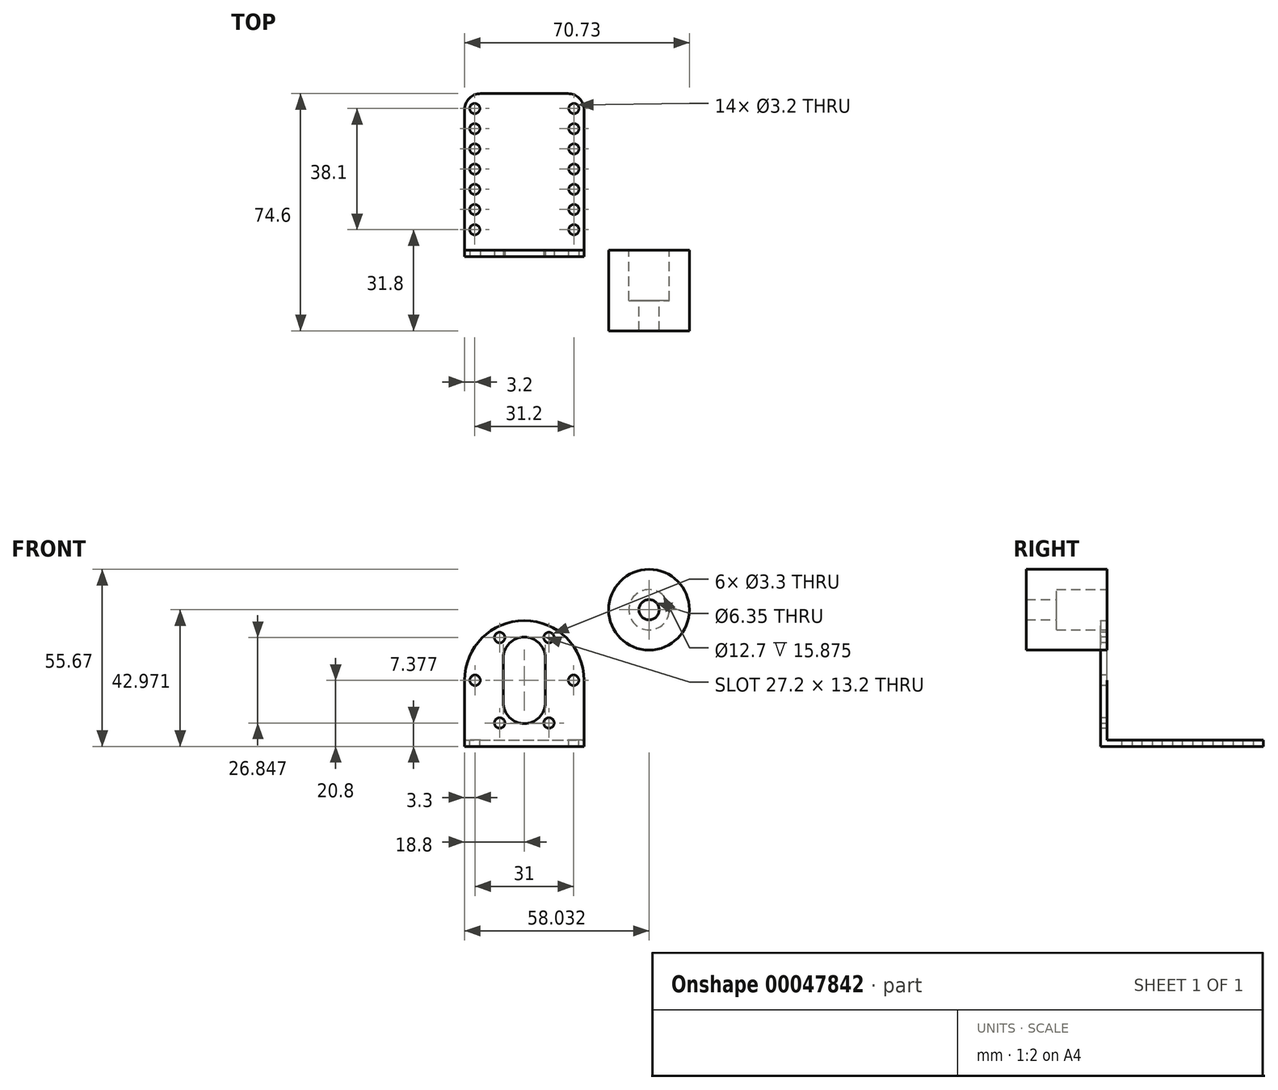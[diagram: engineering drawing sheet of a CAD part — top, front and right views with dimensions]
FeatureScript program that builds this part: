
annotation { "Feature Type Name" : "Feature", "Feature Type Description" : "" }
export const myFeature = defineFeature(function(context is Context, id is Id, definition is map)
    precondition{}
    {
        {
            var Q0;
            Q0=qCreatedBy(makeId("Front.planeOp"),FACE);
            var sketch = newSketch(context, id + "F0", { "sketchPlane" : qUnion([Q0])});
            skLineSegment(sketch, "E0.bottom", {"start": v(-18.8, 0) * mm, "end": v(18.8, 0) * mm});
            skLineSegment(sketch, "E0.top", {"start": v(-18.8, 18.8) * mm, "end": v(18.8, 18.8) * mm, "construction": true});
            skLineSegment(sketch, "E0.left", {"start": v(-18.8, 0) * mm, "end": v(-18.8, 18.8) * mm});
            skLineSegment(sketch, "E0.right", {"start": v(18.8, 0) * mm, "end": v(18.8, 18.8) * mm});
            skArc(sketch, "E1", {"start": v(18.8, 18.8) * mm, "mid": v(0, 37.6) * mm, "end": v(-18.8, 18.8) * mm});
            skSolve(sketch);
        }
        {
            var Q0;
            Q0=makeQuery(id+"F0.imprint","IMPRINT",FACE,{"disambiguationData":[TD([[makeQuery(id+"F0.imprint","IMPRINT",EDGE,{"derivedFrom":sQuery(id+"F0.wireOp",EDGE,"E0.bottom")}),1.0]])]});
            extrude(context, id + "F1", {"entities" : qUnion([Q0]), "depth" : 2 * mm});
        }
        {
            var Q0;
            Q0=makeQuery(id+"F1.opExtrude","CAP_FACE",FACE,{"disambiguationData":[OSD([sQuery(id+"F0.wireOp",EDGE,"E0.bottom"),sQuery(id+"F0.wireOp",EDGE,"E0.left"),sQuery(id+"F0.wireOp",EDGE,"E0.right"),sQuery(id+"F0.wireOp",EDGE,"E1")])],"isStart":false});
            var sketch = newSketch(context, id + "F2", { "sketchPlane" : qUnion([Q0])});
            skCircle(sketch, "E2", {"center": v(0, 18.8) * mm, "radius": 15.5 * mm, "construction": true});
            skLineSegment(sketch, "E3", {"start": v(-18.8, 18.8) * mm, "end": v(18.8, 18.8) * mm, "construction": true});
            skCircle(sketch, "E4", {"center": v(-15.5, 18.8) * mm, "radius": 1.65 * mm});
            skCircle(sketch, "E5.1.0", {"center": v(-7.75, 5.38) * mm, "radius": 1.65 * mm});
            skCircle(sketch, "E5.2.0", {"center": v(7.75, 5.38) * mm, "radius": 1.65 * mm});
            skCircle(sketch, "E5.3.0", {"center": v(15.5, 18.8) * mm, "radius": 1.65 * mm});
            skCircle(sketch, "E5.4.0", {"center": v(7.75, 32.22) * mm, "radius": 1.65 * mm});
            skCircle(sketch, "E5.5.0", {"center": v(-7.75, 32.22) * mm, "radius": 1.65 * mm});
            skSolve(sketch);
        }
        {
            var Q0;
            Q0=makeQuery(id+"F2.imprint","IMPRINT",FACE,{"disambiguationData":[TD([[makeQuery(id+"F2.imprint","IMPRINT",EDGE,{"derivedFrom":sQuery(id+"F2.wireOp",EDGE,"E4")}),1.0]])]});
            var Q1;
            Q1=makeQuery(id+"F2.imprint","IMPRINT",FACE,{"disambiguationData":[TD([[makeQuery(id+"F2.imprint","IMPRINT",EDGE,{"derivedFrom":sQuery(id+"F2.wireOp",EDGE,"E5.5.0")}),1.0]])]});
            var Q2;
            Q2=makeQuery(id+"F2.imprint","IMPRINT",FACE,{"disambiguationData":[TD([[makeQuery(id+"F2.imprint","IMPRINT",EDGE,{"derivedFrom":sQuery(id+"F2.wireOp",EDGE,"E5.4.0")}),1.0]])]});
            var Q3;
            Q3=makeQuery(id+"F2.imprint","IMPRINT",FACE,{"disambiguationData":[TD([[makeQuery(id+"F2.imprint","IMPRINT",EDGE,{"derivedFrom":sQuery(id+"F2.wireOp",EDGE,"E5.2.0")}),1.0]])]});
            var Q4;
            Q4=makeQuery(id+"F2.imprint","IMPRINT",FACE,{"disambiguationData":[TD([[makeQuery(id+"F2.imprint","IMPRINT",EDGE,{"derivedFrom":sQuery(id+"F2.wireOp",EDGE,"E5.1.0")}),1.0]])]});
            var Q5;
            Q5=makeQuery(id+"F2.imprint","IMPRINT",FACE,{"disambiguationData":[TD([[makeQuery(id+"F2.imprint","IMPRINT",EDGE,{"derivedFrom":sQuery(id+"F2.wireOp",EDGE,"E5.3.0")}),1.0]])]});
            extrude(context, id + "F3", {"entities" : qUnion([Q0, Q1, Q2, Q3, Q4, Q5]), "operationType" : NewBodyOperationType.REMOVE, "endBound" : BoundingType.UP_TO_NEXT, "oppositeDirection" : true, "depth" : 25.4 * mm});
        }
        {
            var Q0;
            Q0=makeQuery(id+"F1.opExtrude","CAP_FACE",FACE,{"disambiguationData":[OSD([sQuery(id+"F0.wireOp",EDGE,"E0.bottom"),sQuery(id+"F0.wireOp",EDGE,"E0.left"),sQuery(id+"F0.wireOp",EDGE,"E0.right"),sQuery(id+"F0.wireOp",EDGE,"E1")])],"isStart":false});
            var sketch = newSketch(context, id + "F4", { "sketchPlane" : qUnion([Q0])});
            skLineSegment(sketch, "E6.bottom", {"start": v(-6.6, 25.8) * mm, "end": v(6.6, 25.8) * mm, "construction": true});
            skLineSegment(sketch, "E6.top", {"start": v(-6.6, 11.8) * mm, "end": v(6.6, 11.8) * mm, "construction": true});
            skLineSegment(sketch, "E6.left", {"start": v(-6.6, 25.8) * mm, "end": v(-6.6, 11.8) * mm});
            skLineSegment(sketch, "E6.right", {"start": v(6.6, 25.8) * mm, "end": v(6.6, 11.8) * mm});
            skLineSegment(sketch, "E7", {"start": v(0, 25.8) * mm, "end": v(0, 11.8) * mm, "construction": true});
            skArc(sketch, "E8", {"start": v(6.6, 25.8) * mm, "mid": v(0, 32.4) * mm, "end": v(-6.6, 25.8) * mm});
            skArc(sketch, "E9", {"start": v(-6.6, 11.8) * mm, "mid": v(0, 5.2) * mm, "end": v(6.6, 11.8) * mm});
            skLineSegment(sketch, "E10", {"start": v(-6.6, 18.8) * mm, "end": v(6.6, 18.8) * mm, "construction": true});
            skLineSegment(sketch, "E11", {"start": v(-15.5, 18.8) * mm, "end": v(15.5, 18.8) * mm, "construction": true});
            skSolve(sketch);
        }
        {
            var Q0;
            Q0=makeQuery(id+"F4.imprint","IMPRINT",FACE,{"disambiguationData":[TD([[makeQuery(id+"F4.imprint","IMPRINT",EDGE,{"derivedFrom":sQuery(id+"F4.wireOp",EDGE,"E6.left")}),1.0]])]});
            extrude(context, id + "F5", {"entities" : qUnion([Q0]), "operationType" : NewBodyOperationType.REMOVE, "endBound" : BoundingType.UP_TO_NEXT, "oppositeDirection" : true, "depth" : 25.4 * mm});
        }
        {
            var Q0;
            Q0=qCreatedBy(makeId("Top.planeOp"),FACE);
            var sketch = newSketch(context, id + "F6", { "sketchPlane" : qUnion([Q0])});
            skLineSegment(sketch, "E12.top", {"start": v(-18.8, 49.2) * mm, "end": v(18.8, 49.2) * mm});
            skLineSegment(sketch, "E12.left", {"start": v(-18.8, -2) * mm, "end": v(-18.8, 49.2) * mm});
            skLineSegment(sketch, "E12.right", {"start": v(18.8, -2) * mm, "end": v(18.8, 49.2) * mm});
            skLineSegment(sketch, "E13.0", {"start": v(-18.8, -2) * mm, "end": v(18.8, -2) * mm});
            skSolve(sketch);
        }
        {
            var Q0;
            Q0=makeQuery(id+"F6.imprint","IMPRINT",FACE,{"disambiguationData":[TD([[makeQuery(id+"F6.imprint","IMPRINT",EDGE,{"derivedFrom":sQuery(id+"F6.wireOp",EDGE,"E12.top")}),-1.0]])]});
            extrude(context, id + "F7", {"entities" : qUnion([Q0]), "operationType" : NewBodyOperationType.ADD, "oppositeDirection" : true, "depth" : 2 * mm});
        }
        {
            var Q0;
            Q0=makeQuery(id+"F7.opExtrude","CAP_FACE",FACE,{"disambiguationData":[OSD([sQuery(id+"F6.wireOp",EDGE,"E12.top"),sQuery(id+"F6.wireOp",EDGE,"E12.left"),sQuery(id+"F6.wireOp",EDGE,"E12.right"),sQuery(id+"F6.wireOp",EDGE,"E13.0")])],"isStart":true});
            var sketch = newSketch(context, id + "F8", { "sketchPlane" : qUnion([Q0])});
            skLineSegment(sketch, "E14.bottom", {"start": v(-15.6, 44.5) * mm, "end": v(15.6, 44.5) * mm, "construction": true});
            skLineSegment(sketch, "E14.top", {"start": v(-15.6, 6.4) * mm, "end": v(15.6, 6.4) * mm, "construction": true});
            skLineSegment(sketch, "E14.left", {"start": v(-15.6, 44.5) * mm, "end": v(-15.6, 6.4) * mm, "construction": true});
            skLineSegment(sketch, "E14.right", {"start": v(15.6, 44.5) * mm, "end": v(15.6, 6.4) * mm, "construction": true});
            skLineSegment(sketch, "E15", {"start": v(0, 44.5) * mm, "end": v(0, 6.4) * mm, "construction": true});
            skCircle(sketch, "E16", {"center": v(-15.6, 6.4) * mm, "radius": 1.6 * mm});
            skCircle(sketch, "E17.0.1.0", {"center": v(-15.6, 12.75) * mm, "radius": 1.6 * mm});
            skCircle(sketch, "E17.0.2.0", {"center": v(-15.6, 19.1) * mm, "radius": 1.6 * mm});
            skCircle(sketch, "E17.0.3.0", {"center": v(-15.6, 25.45) * mm, "radius": 1.6 * mm});
            skCircle(sketch, "E17.0.4.0", {"center": v(-15.6, 31.8) * mm, "radius": 1.6 * mm});
            skCircle(sketch, "E17.0.5.0", {"center": v(-15.6, 38.15) * mm, "radius": 1.6 * mm});
            skCircle(sketch, "E17.0.6.0", {"center": v(-15.6, 44.5) * mm, "radius": 1.6 * mm});
            skCircle(sketch, "E17.1.0.0", {"center": v(15.6, 6.4) * mm, "radius": 1.6 * mm});
            skCircle(sketch, "E17.1.1.0", {"center": v(15.6, 12.75) * mm, "radius": 1.6 * mm});
            skCircle(sketch, "E17.1.2.0", {"center": v(15.6, 19.1) * mm, "radius": 1.6 * mm});
            skCircle(sketch, "E17.1.3.0", {"center": v(15.6, 25.45) * mm, "radius": 1.6 * mm});
            skCircle(sketch, "E17.1.4.0", {"center": v(15.6, 31.8) * mm, "radius": 1.6 * mm});
            skCircle(sketch, "E17.1.5.0", {"center": v(15.6, 38.15) * mm, "radius": 1.6 * mm});
            skCircle(sketch, "E17.1.6.0", {"center": v(15.6, 44.5) * mm, "radius": 1.6 * mm});
            skLineSegment(sketch, "E17.direction2", {"start": v(-15.6, 6.4) * mm, "end": v(-15.6, 12.75) * mm, "construction": true});
            skSolve(sketch);
        }
        {
            var Q0;
            Q0=makeQuery(id+"F8.imprint","IMPRINT",FACE,{"disambiguationData":[TD([[makeQuery(id+"F8.imprint","IMPRINT",EDGE,{"derivedFrom":sQuery(id+"F8.wireOp",EDGE,"E17.0.6.0")}),1.0]])]});
            var Q1;
            Q1=makeQuery(id+"F8.imprint","IMPRINT",FACE,{"disambiguationData":[TD([[makeQuery(id+"F8.imprint","IMPRINT",EDGE,{"derivedFrom":sQuery(id+"F8.wireOp",EDGE,"E17.0.5.0")}),1.0]])]});
            var Q2;
            Q2=makeQuery(id+"F8.imprint","IMPRINT",FACE,{"disambiguationData":[TD([[makeQuery(id+"F8.imprint","IMPRINT",EDGE,{"derivedFrom":sQuery(id+"F8.wireOp",EDGE,"E17.0.4.0")}),1.0]])]});
            var Q3;
            Q3=makeQuery(id+"F8.imprint","IMPRINT",FACE,{"disambiguationData":[TD([[makeQuery(id+"F8.imprint","IMPRINT",EDGE,{"derivedFrom":sQuery(id+"F8.wireOp",EDGE,"E17.0.3.0")}),1.0]])]});
            var Q4;
            Q4=makeQuery(id+"F8.imprint","IMPRINT",FACE,{"disambiguationData":[TD([[makeQuery(id+"F8.imprint","IMPRINT",EDGE,{"derivedFrom":sQuery(id+"F8.wireOp",EDGE,"E17.0.2.0")}),1.0]])]});
            var Q5;
            Q5=makeQuery(id+"F8.imprint","IMPRINT",FACE,{"disambiguationData":[TD([[makeQuery(id+"F8.imprint","IMPRINT",EDGE,{"derivedFrom":sQuery(id+"F8.wireOp",EDGE,"E17.0.1.0")}),1.0]])]});
            var Q6;
            Q6=makeQuery(id+"F8.imprint","IMPRINT",FACE,{"disambiguationData":[TD([[makeQuery(id+"F8.imprint","IMPRINT",EDGE,{"derivedFrom":sQuery(id+"F8.wireOp",EDGE,"E16")}),1.0]])]});
            var Q7;
            Q7=makeQuery(id+"F8.imprint","IMPRINT",FACE,{"disambiguationData":[TD([[makeQuery(id+"F8.imprint","IMPRINT",EDGE,{"derivedFrom":sQuery(id+"F8.wireOp",EDGE,"E17.1.6.0")}),1.0]])]});
            var Q8;
            Q8=makeQuery(id+"F8.imprint","IMPRINT",FACE,{"disambiguationData":[TD([[makeQuery(id+"F8.imprint","IMPRINT",EDGE,{"derivedFrom":sQuery(id+"F8.wireOp",EDGE,"E17.1.5.0")}),1.0]])]});
            var Q9;
            Q9=makeQuery(id+"F8.imprint","IMPRINT",FACE,{"disambiguationData":[TD([[makeQuery(id+"F8.imprint","IMPRINT",EDGE,{"derivedFrom":sQuery(id+"F8.wireOp",EDGE,"E17.1.4.0")}),1.0]])]});
            var Q10;
            Q10=makeQuery(id+"F8.imprint","IMPRINT",FACE,{"disambiguationData":[TD([[makeQuery(id+"F8.imprint","IMPRINT",EDGE,{"derivedFrom":sQuery(id+"F8.wireOp",EDGE,"E17.1.3.0")}),1.0]])]});
            var Q11;
            Q11=makeQuery(id+"F8.imprint","IMPRINT",FACE,{"disambiguationData":[TD([[makeQuery(id+"F8.imprint","IMPRINT",EDGE,{"derivedFrom":sQuery(id+"F8.wireOp",EDGE,"E17.1.2.0")}),1.0]])]});
            var Q12;
            Q12=makeQuery(id+"F8.imprint","IMPRINT",FACE,{"disambiguationData":[TD([[makeQuery(id+"F8.imprint","IMPRINT",EDGE,{"derivedFrom":sQuery(id+"F8.wireOp",EDGE,"E17.1.1.0")}),1.0]])]});
            var Q13;
            Q13=makeQuery(id+"F8.imprint","IMPRINT",FACE,{"disambiguationData":[TD([[makeQuery(id+"F8.imprint","IMPRINT",EDGE,{"derivedFrom":sQuery(id+"F8.wireOp",EDGE,"E17.1.0.0")}),1.0]])]});
            extrude(context, id + "F9", {"entities" : qUnion([Q0, Q1, Q2, Q3, Q4, Q5, Q6, Q7, Q8, Q9, Q10, Q11, Q12, Q13]), "operationType" : NewBodyOperationType.REMOVE, "endBound" : BoundingType.UP_TO_NEXT, "oppositeDirection" : true, "depth" : 25.4 * mm});
        }
        {
            var Q0;
            Q0=makeQuery(id+"F7.opExtrude","SWEPT_EDGE",EDGE,{"disambiguationData":[OSD([sQuery(id+"F6.wireOp",EDGE,"E12.top"),sQuery(id+"F6.wireOp",EDGE,"E12.left")])]});
            var Q1;
            Q1=makeQuery(id+"F7.opExtrude","SWEPT_EDGE",EDGE,{"disambiguationData":[OSD([sQuery(id+"F6.wireOp",EDGE,"E12.top"),sQuery(id+"F6.wireOp",EDGE,"E12.right")])]});
            fillet(context, id + "F10", {"entities" : qUnion([Q0, Q1]), "radius" : 5.08 * mm, "tangentPropagation" : true, "allowEdgeOverflow" : false});
        }
        {
            var Q0;
            Q0=qCreatedBy(makeId("Front.planeOp"),FACE);
            var sketch = newSketch(context, id + "F11", { "sketchPlane" : qUnion([Q0])});
            skCircle(sketch, "E18", {"center": v(39.23, 40.97) * mm, "radius": 12.7 * mm});
            skSolve(sketch);
        }
        {
            var Q0;
            Q0=makeQuery(id+"F11.imprint","IMPRINT",FACE,{"disambiguationData":[TD([[makeQuery(id+"F11.imprint","IMPRINT",EDGE,{"derivedFrom":sQuery(id+"F11.wireOp",EDGE,"E18")}),1.0]])]});
            extrude(context, id + "F12", {"entities" : qUnion([Q0]), "depth" : 25.4 * mm});
        }
        {
            var Q0;
            Q0=sQuery(id+"F11.wireOp",VERTEX,"E18.center");
            var Q1;
            Q1=makeQuery(id+"F12.opExtrude","SWEPT_BODY",BODY,{"disambiguationData":[OSD([sQuery(id+"F11.wireOp",EDGE,"E18")])]});
            hole(context, id + "F13", {"style" : HoleStyle.SIMPLE, "holeDiameter" : 6.35 * mm, "endStyle" : HoleEndStyle.THROUGH, "oppositeDirection" : true, "locations" : qUnion([Q0]), "scope" : qUnion([Q1])});
        }
        {
            var Q0;
            Q0=makeQuery(id+"F11.imprint","IMPRINT",FACE,{"disambiguationData":[TD([[makeQuery(id+"F11.imprint","IMPRINT",EDGE,{"derivedFrom":sQuery(id+"F11.wireOp",EDGE,"E18")}),1.0]])]});
            var sketch = newSketch(context, id + "F14", { "sketchPlane" : qUnion([Q0])});
            skPoint(sketch, "E19.0", {"position": v(39.23, 40.97) * mm});
            skCircle(sketch, "E20", {"center": v(39.23, 40.97) * mm, "radius": 6.35 * mm});
            skSolve(sketch);
        }
        {
            var Q0;
            Q0=makeQuery(id+"F14.imprint","IMPRINT",FACE,{"disambiguationData":[TD([[makeQuery(id+"F14.imprint","IMPRINT",EDGE,{"derivedFrom":sQuery(id+"F14.wireOp",EDGE,"E20")}),1.0]])]});
            extrude(context, id + "F15", {"entities" : qUnion([Q0]), "operationType" : NewBodyOperationType.REMOVE, "depth" : 15.88 * mm});
        }
    });
